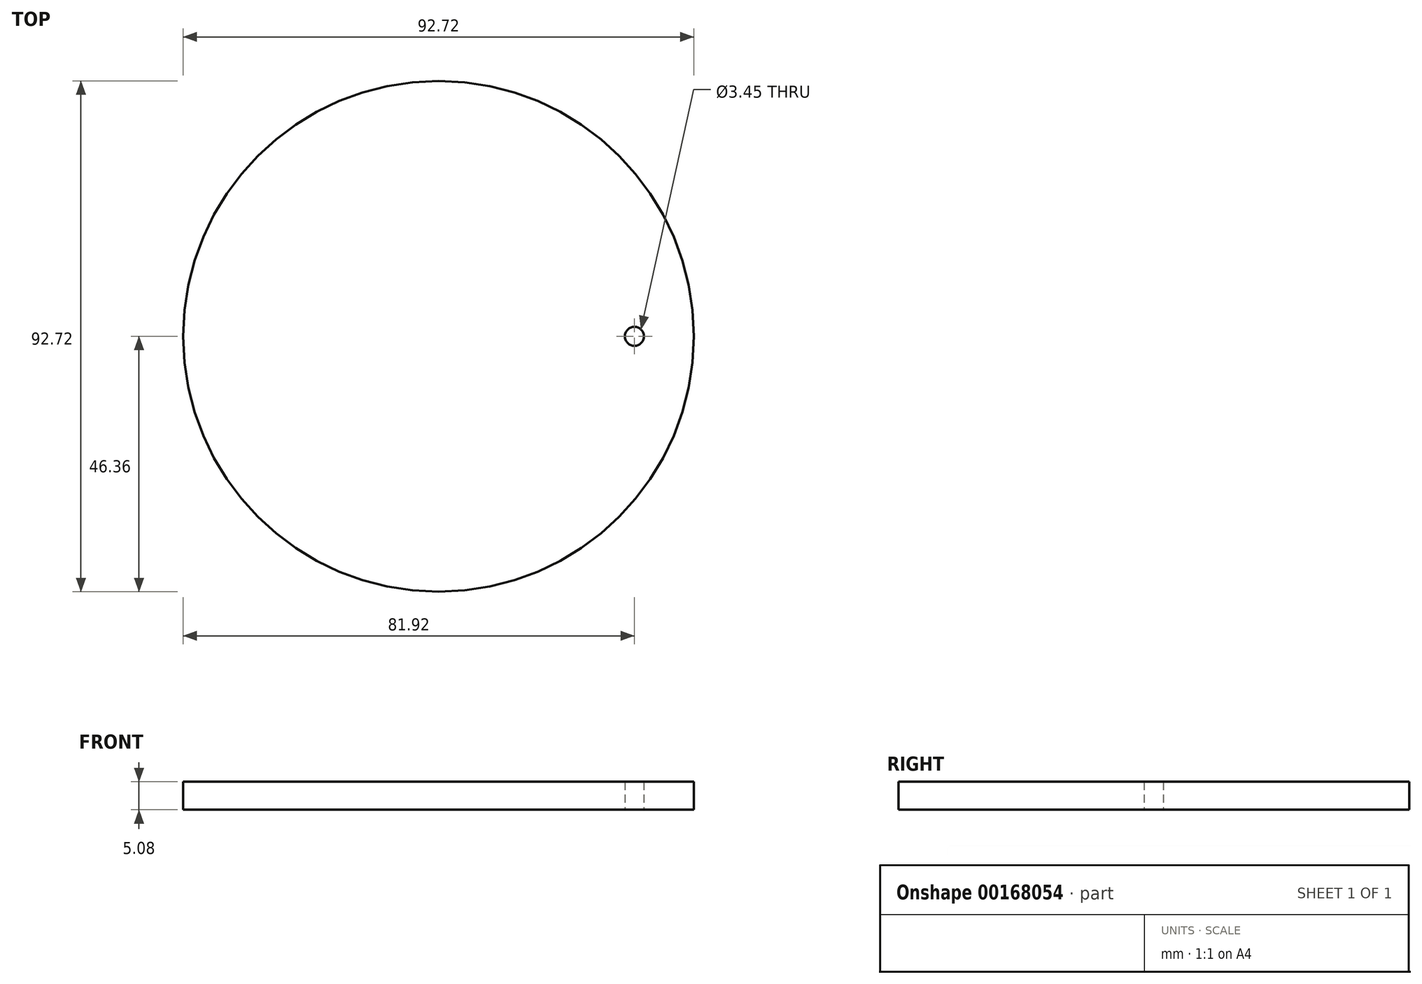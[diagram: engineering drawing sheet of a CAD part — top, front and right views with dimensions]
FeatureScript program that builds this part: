
annotation { "Feature Type Name" : "Feature", "Feature Type Description" : "" }
export const myFeature = defineFeature(function(context is Context, id is Id, definition is map)
    precondition{}
    {
        {
            var Q0;
            Q0=qCreatedBy(makeId("Top.planeOp"),FACE);
            var sketch = newSketch(context, id + "F0", { "sketchPlane" : qUnion([Q0])});
            skCircle(sketch, "E0", {"center": v(0, 0) * mm, "radius": 46.35 * mm});
            skSolve(sketch);
        }
        {
            var Q0;
            Q0=qSketchRegion(id+"F0",true);
            extrude(context, id + "F1", {"entities" : qUnion([Q0]), "depth" : 5.08 * mm});
        }
        {
            var Q0;
            Q0=makeQuery(id+"F1.opExtrude","CAP_FACE",FACE,{"disambiguationData":[OSD([sQuery(id+"F0.wireOp",EDGE,"E0")])],"isStart":true});
            var sketch = newSketch(context, id + "F2", { "sketchPlane" : qUnion([Q0])});
            skPoint(sketch, "E1", {"position": v(35.56, 0) * mm});
            skSolve(sketch);
        }
        {
            var Q0;
            Q0=qCreatedBy(makeId("Front.planeOp"),FACE);
            var sketch = newSketch(context, id + "F3", { "sketchPlane" : qUnion([Q0])});
            skLineSegment(sketch, "E2", {"start": v(0, 0) * mm, "end": v(0, 19.52) * mm, "construction": true});
            skSolve(sketch);
        }
        {
            var Q0;
            Q0=sQuery(id+"F2.wireOp",VERTEX,"E1");
            var Q1;
            Q1=makeQuery(id+"F1.opExtrude","SWEPT_BODY",BODY,{"disambiguationData":[OSD([sQuery(id+"F0.wireOp",EDGE,"E0")])]});
            hole(context, id + "F4", {"style" : HoleStyle.SIMPLE, "endStyle" : HoleEndStyle.THROUGH, "standardTappedOrClearance" : lookupTablePath({ "standard" : "ANSI", "engagement" : "75%", "pitch" : "32 tpi", "size" : "#8", "type" : "Tapped" }), "standardBlindInLast" : lookupTablePath({ "standard" : "ANSI", "engagement" : "75%", "pitch" : "32 tpi", "size" : "#8", "type" : "Tapped" }), "holeDiameter" : 3.45 * mm, "locations" : qUnion([Q0]), "scope" : qUnion([Q1]), "isTappedThrough" : true, "majorDiameter" : 4.17 * mm, "showTappedDepth" : true});
        }
    });
